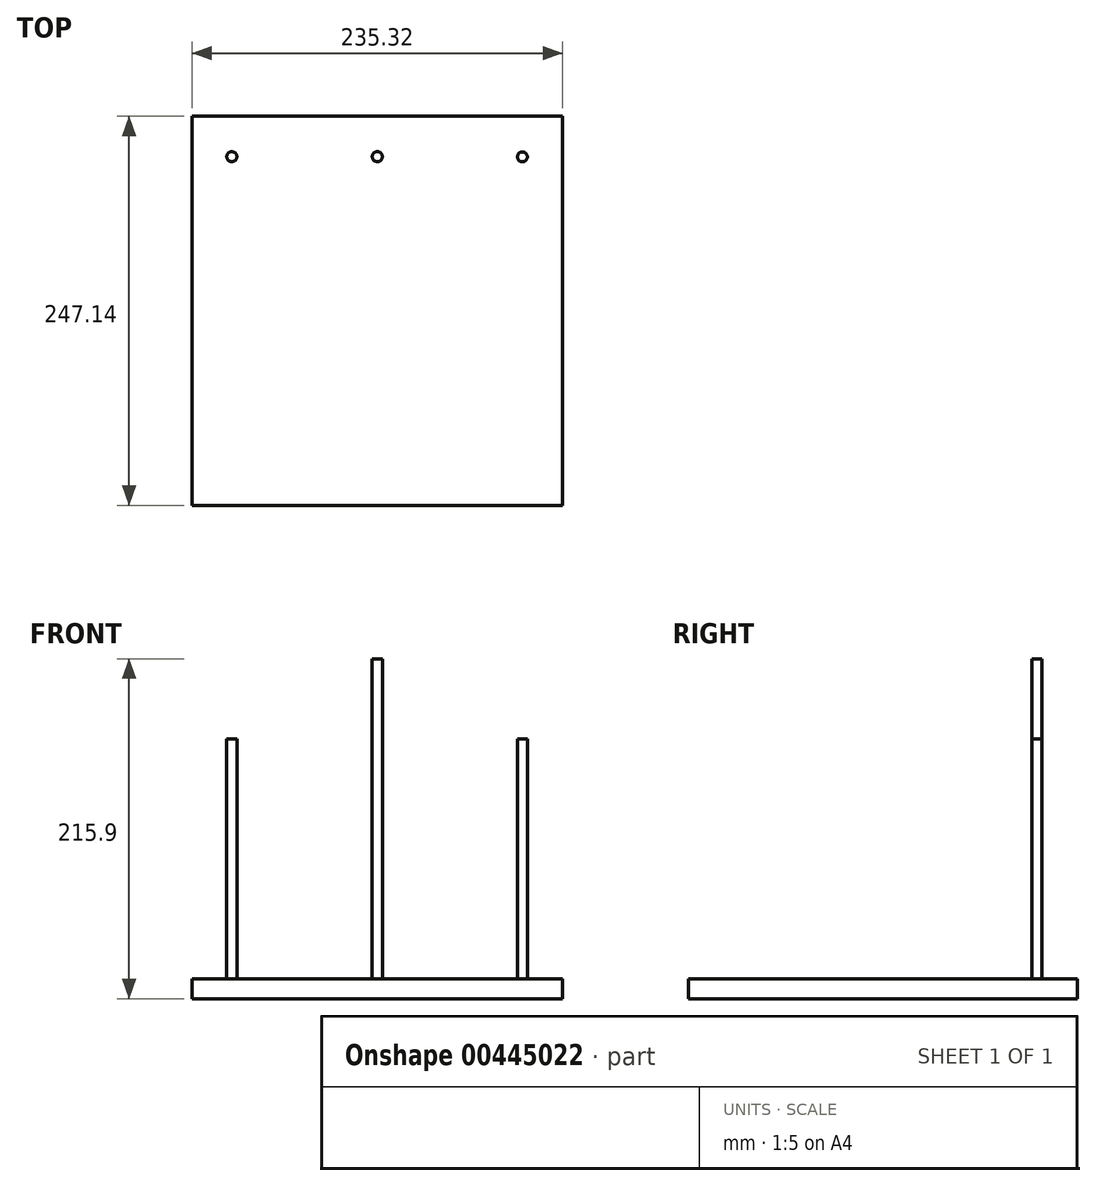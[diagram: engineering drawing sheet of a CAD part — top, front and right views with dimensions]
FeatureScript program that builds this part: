
annotation { "Feature Type Name" : "Feature", "Feature Type Description" : "" }
export const myFeature = defineFeature(function(context is Context, id is Id, definition is map)
    precondition{}
    {
        {
            var Q0;
            Q0=qCreatedBy(makeId("Top.planeOp"),FACE);
            var sketch = newSketch(context, id + "F0", { "sketchPlane" : qUnion([Q0])});
            skLineSegment(sketch, "E0.bottom", {"start": v(-110.83, 99.08) * mm, "end": v(124.5, 99.08) * mm});
            skLineSegment(sketch, "E0.top", {"start": v(-110.83, -148.06) * mm, "end": v(124.5, -148.06) * mm});
            skLineSegment(sketch, "E0.left", {"start": v(-110.83, 99.08) * mm, "end": v(-110.83, -148.06) * mm});
            skLineSegment(sketch, "E0.right", {"start": v(124.5, 99.08) * mm, "end": v(124.5, -148.06) * mm});
            skSolve(sketch);
        }
        {
            var Q0;
            Q0=makeQuery(id+"F0.imprint","IMPRINT",FACE,{"disambiguationData":[TD([[makeQuery(id+"F0.imprint","IMPRINT",EDGE,{"derivedFrom":sQuery(id+"F0.wireOp",EDGE,"E0.bottom")}),-1.0]])]});
            extrude(context, id + "F1", {"entities" : qUnion([Q0]), "oppositeDirection" : true, "depth" : 12.7 * mm});
        }
        {
            var Q0;
            Q0=makeQuery(id+"F1.opExtrude","CAP_FACE",FACE,{"disambiguationData":[OSD([sQuery(id+"F0.wireOp",EDGE,"E0.bottom"),sQuery(id+"F0.wireOp",EDGE,"E0.top"),sQuery(id+"F0.wireOp",EDGE,"E0.left"),sQuery(id+"F0.wireOp",EDGE,"E0.right")])],"isStart":true});
            var sketch = newSketch(context, id + "F2", { "sketchPlane" : qUnion([Q0])});
            skCircle(sketch, "E1", {"center": v(-85.5, 73.35) * mm, "radius": 3.2 * mm});
            skSolve(sketch);
        }
        {
            var Q0;
            Q0=makeQuery(id+"F2.imprint","IMPRINT",FACE,{"disambiguationData":[TD([[makeQuery(id+"F2.imprint","IMPRINT",EDGE,{"derivedFrom":sQuery(id+"F2.wireOp",EDGE,"E1")}),1.0]])]});
            extrude(context, id + "F3", {"entities" : qUnion([Q0]), "operationType" : NewBodyOperationType.ADD, "depth" : 152.4 * mm});
        }
        {
            var Q0;
            Q0=makeQuery(id+"F1.opExtrude","CAP_FACE",FACE,{"disambiguationData":[OSD([sQuery(id+"F0.wireOp",EDGE,"E0.bottom"),sQuery(id+"F0.wireOp",EDGE,"E0.top"),sQuery(id+"F0.wireOp",EDGE,"E0.left"),sQuery(id+"F0.wireOp",EDGE,"E0.right")])],"isStart":true});
            var sketch = newSketch(context, id + "F4", { "sketchPlane" : qUnion([Q0])});
            skCircle(sketch, "E2", {"center": v(99.04, 73.24) * mm, "radius": 3.16 * mm});
            skSolve(sketch);
        }
        {
            var Q0;
            Q0 = qSketchRegion(id + "F4", true);
            extrude(context, id + "F5", {"entities" : qUnion([Q0]), "operationType" : NewBodyOperationType.ADD, "depth" : 152.4 * mm});
        }
        {
            var Q0;
            Q0=makeQuery(id+"F1.opExtrude","CAP_FACE",FACE,{"disambiguationData":[OSD([sQuery(id+"F0.wireOp",EDGE,"E0.bottom"),sQuery(id+"F0.wireOp",EDGE,"E0.top"),sQuery(id+"F0.wireOp",EDGE,"E0.left"),sQuery(id+"F0.wireOp",EDGE,"E0.right")])],"isStart":true});
            var sketch = newSketch(context, id + "F6", { "sketchPlane" : qUnion([Q0])});
            skCircle(sketch, "E3", {"center": v(6.92, 73.35) * mm, "radius": 3.21 * mm});
            skSolve(sketch);
        }
        {
            var Q0;
            Q0 = qSketchRegion(id + "F6", true);
            extrude(context, id + "F7", {"entities" : qUnion([Q0]), "operationType" : NewBodyOperationType.ADD, "depth" : 203.2 * mm});
        }
    });
